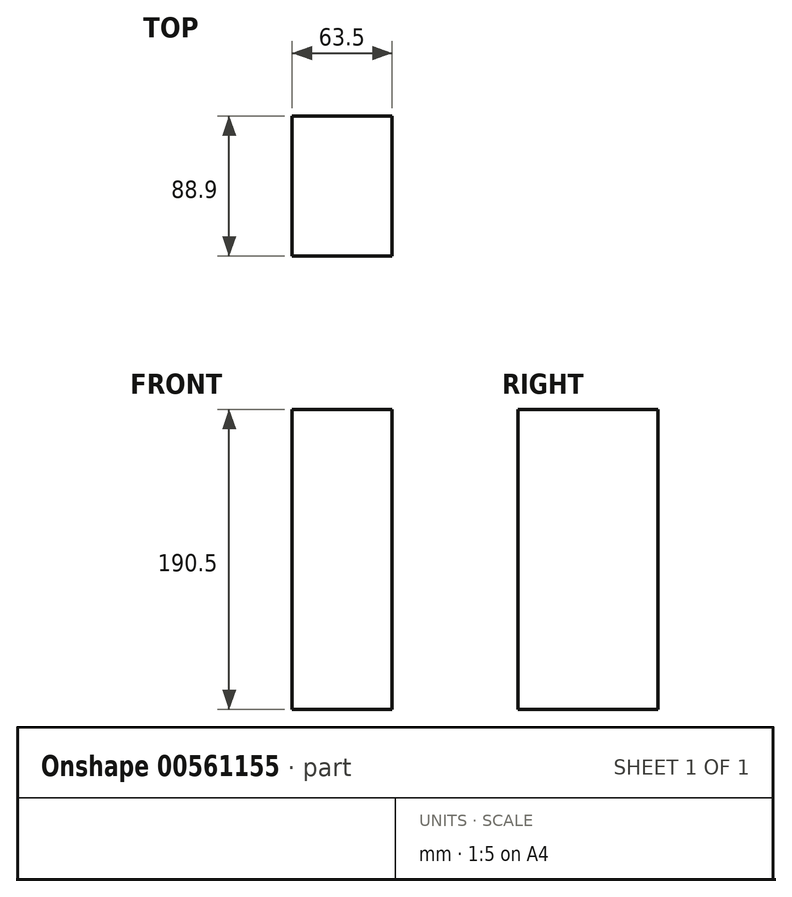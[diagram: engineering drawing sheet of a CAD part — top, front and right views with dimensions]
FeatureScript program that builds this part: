
annotation { "Feature Type Name" : "Feature", "Feature Type Description" : "" }
export const myFeature = defineFeature(function(context is Context, id is Id, definition is map)
    precondition{}
    {
        {
            var Q0;
            Q0=qCreatedBy(makeId("Top.planeOp"),FACE);
            var sketch = newSketch(context, id + "F0", { "sketchPlane" : qUnion([Q0])});
            skLineSegment(sketch, "E0", {"start": v(0, 0) * mm, "end": v(63.5, 0) * mm});
            skLineSegment(sketch, "E1", {"start": v(63.5, 0) * mm, "end": v(63.5, -88.9) * mm});
            skLineSegment(sketch, "E2", {"start": v(63.5, -88.9) * mm, "end": v(0, -88.9) * mm});
            skLineSegment(sketch, "E3", {"start": v(0, -88.9) * mm, "end": v(0, 0) * mm});
            skSolve(sketch);
        }
        {
            var Q0;
            Q0 = qSketchRegion(id + "F0", true);
            extrude(context, id + "F1", {"entities" : qUnion([Q0]), "depth" : 190.5 * mm, "offsetDistance" : 25.4 * mm});
        }
    });
